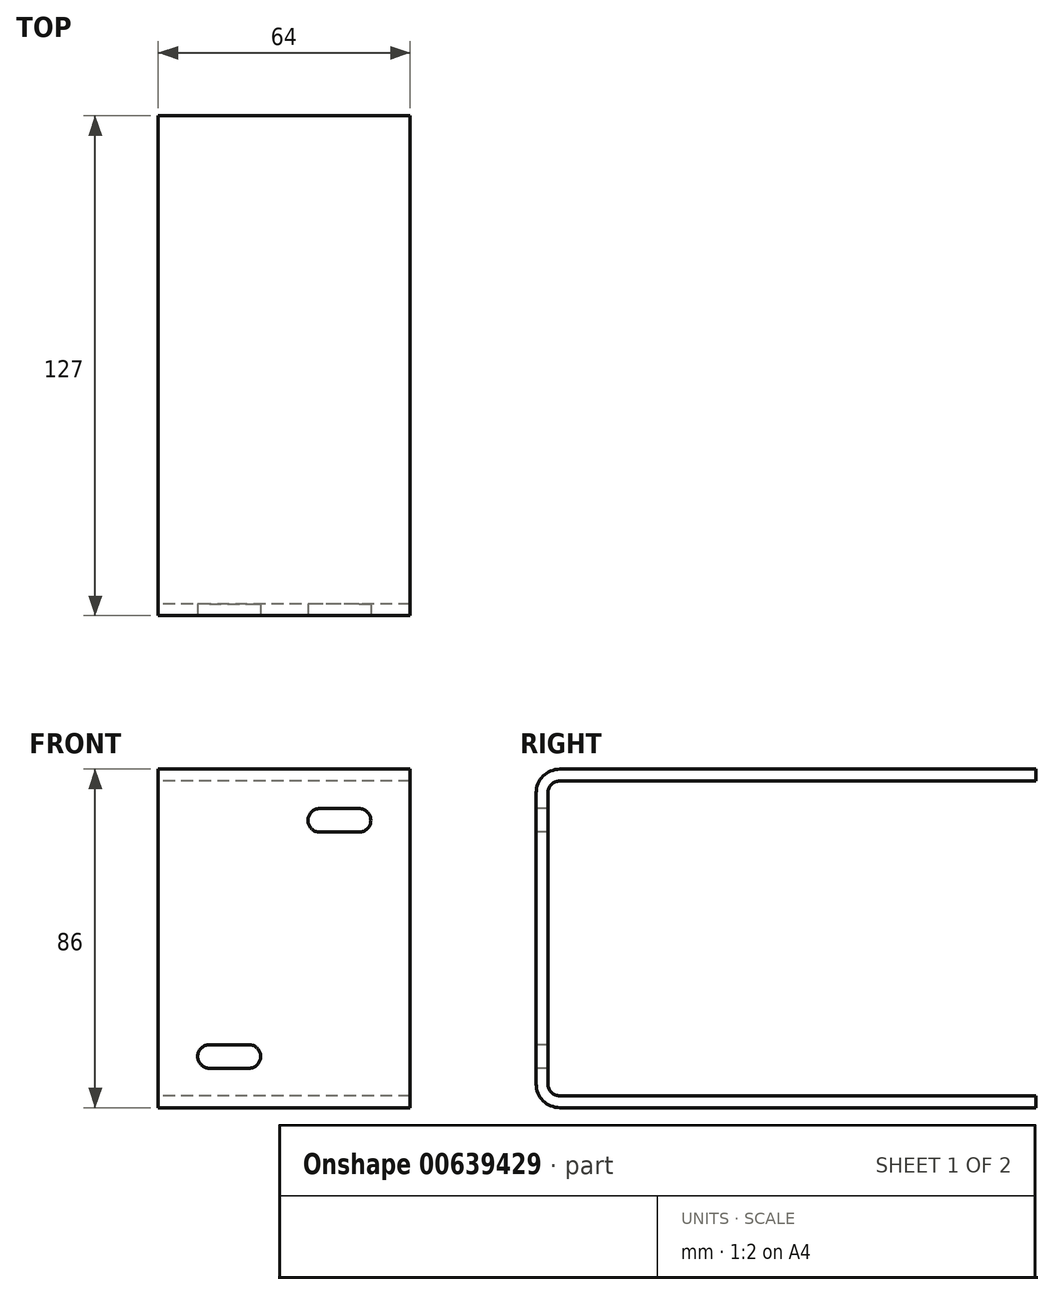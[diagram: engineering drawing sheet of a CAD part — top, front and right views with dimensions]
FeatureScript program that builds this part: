
annotation { "Feature Type Name" : "Feature", "Feature Type Description" : "" }
export const myFeature = defineFeature(function(context is Context, id is Id, definition is map)
    precondition{}
    {
        {
            var Q0;
            Q0=qCreatedBy(makeId("Right.planeOp"),FACE);
            var sketch = newSketch(context, id + "F0", { "sketchPlane" : qUnion([Q0])});
            skLineSegment(sketch, "E0", {"start": v(0, 6) * mm, "end": v(0, 80) * mm});
            skLineSegment(sketch, "E1", {"start": v(6, 86) * mm, "end": v(127, 86) * mm});
            skLineSegment(sketch, "E2", {"start": v(6, 0) * mm, "end": v(127, 0) * mm});
            skLineSegment(sketch, "E3.0", {"start": v(6, 83) * mm, "end": v(127, 83) * mm});
            skLineSegment(sketch, "E3.1", {"start": v(3, 6) * mm, "end": v(3, 80) * mm});
            skLineSegment(sketch, "E3.2", {"start": v(6, 3) * mm, "end": v(127, 3) * mm});
            skPoint(sketch, "E4.visualSharp", {"position": v(3, 83) * mm});
            skArc(sketch, "E4.filletArc", {"start": v(6, 83) * mm, "mid": v(3.88, 82.12) * mm, "end": v(3, 80) * mm});
            skPoint(sketch, "E5.visualSharp", {"position": v(3, 3) * mm});
            skArc(sketch, "E5.filletArc", {"start": v(3, 6) * mm, "mid": v(3.88, 3.88) * mm, "end": v(6, 3) * mm});
            skPoint(sketch, "E6.visualSharp", {"position": v(0, 86) * mm});
            skArc(sketch, "E6.filletArc", {"start": v(6, 86) * mm, "mid": v(1.76, 84.24) * mm, "end": v(0, 80) * mm});
            skPoint(sketch, "E7.visualSharp", {"position": v(0, 0) * mm});
            skArc(sketch, "E7.filletArc", {"start": v(0, 6) * mm, "mid": v(1.76, 1.76) * mm, "end": v(6, 0) * mm});
            skLineSegment(sketch, "E8", {"start": v(127, 83) * mm, "end": v(127, 86) * mm});
            skLineSegment(sketch, "E9", {"start": v(127, 3) * mm, "end": v(127, 0) * mm});
            skSolve(sketch);
        }
        {
            var Q0;
            Q0=makeQuery(id+"F0.imprint","IMPRINT",FACE,{"disambiguationData":[TD([[makeQuery(id+"F0.imprint","IMPRINT",EDGE,{"derivedFrom":sQuery(id+"F0.wireOp",EDGE,"E0")}),-1.0]])]});
            extrude(context, id + "F1", {"entities" : qUnion([Q0]), "depth" : 64 * mm, "offsetDistance" : 25 * mm});
        }
        {
            var Q0;
            Q0=makeQuery(id+"F1.opExtrude","SWEPT_FACE",FACE,{"disambiguationData":[OSD([sQuery(id+"F0.wireOp",EDGE,"E0")])]});
            var sketch = newSketch(context, id + "F2", { "sketchPlane" : qUnion([Q0])});
            skLineSegment(sketch, "E10", {"start": v(0, 43) * mm, "end": v(64, 43) * mm, "construction": true});
            skLineSegment(sketch, "E11", {"start": v(41, 76) * mm, "end": v(51, 76) * mm});
            skArc(sketch, "E12", {"start": v(51, 70) * mm, "mid": v(54, 73) * mm, "end": v(51, 76) * mm});
            skLineSegment(sketch, "E13", {"start": v(51, 70) * mm, "end": v(41, 70) * mm});
            skArc(sketch, "E14", {"start": v(41, 76) * mm, "mid": v(38, 73) * mm, "end": v(41, 70) * mm});
            skLineSegment(sketch, "E15", {"start": v(46, 76) * mm, "end": v(46, 70) * mm, "construction": true});
            skPoint(sketch, "E16.endSnap0", {"position": v(46, 73) * mm});
            skLineSegment(sketch, "E17", {"start": v(32, 80) * mm, "end": v(32, 6) * mm, "construction": true});
            skPoint(sketch, "E18.MirrorP", {"position": v(18, 73) * mm});
            skArc(sketch, "E19.MirrorCS", {"start": v(13, 70) * mm, "mid": v(10, 73) * mm, "end": v(13, 76) * mm});
            skLineSegment(sketch, "E20.MirrorCS", {"start": v(13, 70) * mm, "end": v(23, 70) * mm});
            skLineSegment(sketch, "E21.MirrorCS", {"start": v(23, 76) * mm, "end": v(13, 76) * mm});
            skArc(sketch, "E22.MirrorCS", {"start": v(23, 76) * mm, "mid": v(26, 73) * mm, "end": v(23, 70) * mm});
            skLineSegment(sketch, "E23.MirrorCS", {"start": v(18, 76) * mm, "end": v(18, 70) * mm, "construction": true});
            skLineSegment(sketch, "E24.MirrorCS", {"start": v(46, 10) * mm, "end": v(46, 16) * mm, "construction": true});
            skLineSegment(sketch, "E25.MirrorCS", {"start": v(18, 10) * mm, "end": v(18, 16) * mm, "construction": true});
            skArc(sketch, "E26.MirrorCS", {"start": v(41, 10) * mm, "mid": v(38, 13) * mm, "end": v(41, 16) * mm});
            skLineSegment(sketch, "E27.MirrorCS", {"start": v(51, 16) * mm, "end": v(41, 16) * mm});
            skArc(sketch, "E28.MirrorCS", {"start": v(51, 16) * mm, "mid": v(54, 13) * mm, "end": v(51, 10) * mm});
            skLineSegment(sketch, "E29.MirrorCS", {"start": v(41, 10) * mm, "end": v(51, 10) * mm});
            skArc(sketch, "E30.MirrorCS", {"start": v(13, 16) * mm, "mid": v(10, 13) * mm, "end": v(13, 10) * mm});
            skArc(sketch, "E31.MirrorCS", {"start": v(23, 10) * mm, "mid": v(26, 13) * mm, "end": v(23, 16) * mm});
            skPoint(sketch, "E32.MirrorP", {"position": v(18, 13) * mm});
            skLineSegment(sketch, "E33.MirrorCS", {"start": v(23, 10) * mm, "end": v(13, 10) * mm});
            skPoint(sketch, "E34.MirrorP", {"position": v(46, 13) * mm});
            skLineSegment(sketch, "E35.MirrorCS", {"start": v(13, 16) * mm, "end": v(23, 16) * mm});
            skSolve(sketch);
        }
        {
            var Q0;
            Q0=makeQuery(id+"F2.imprint","IMPRINT",FACE,{"disambiguationData":[TD([[makeQuery(id+"F2.imprint","IMPRINT",EDGE,{"derivedFrom":sQuery(id+"F2.wireOp",EDGE,"E19.MirrorCS")}),-1.0]])]});
            var Q1;
            Q1=makeQuery(id+"F2.imprint","IMPRINT",FACE,{"disambiguationData":[TD([[makeQuery(id+"F2.imprint","IMPRINT",EDGE,{"derivedFrom":sQuery(id+"F2.wireOp",EDGE,"E11")}),-1.0]])]});
            var Q2;
            Q2=makeQuery(id+"F2.imprint","IMPRINT",FACE,{"disambiguationData":[TD([[makeQuery(id+"F2.imprint","IMPRINT",EDGE,{"derivedFrom":sQuery(id+"F2.wireOp",EDGE,"E26.MirrorCS")}),-1.0]])]});
            var Q3;
            Q3=makeQuery(id+"F2.imprint","IMPRINT",FACE,{"disambiguationData":[TD([[makeQuery(id+"F2.imprint","IMPRINT",EDGE,{"derivedFrom":sQuery(id+"F2.wireOp",EDGE,"E30.MirrorCS")}),1.0]])]});
            extrude(context, id + "F3", {"entities" : qUnion([Q0, Q1, Q2, Q3]), "operationType" : NewBodyOperationType.REMOVE, "endBound" : BoundingType.UP_TO_NEXT, "oppositeDirection" : true, "depth" : 25 * mm, "offsetDistance" : 25 * mm});
        }
    });
